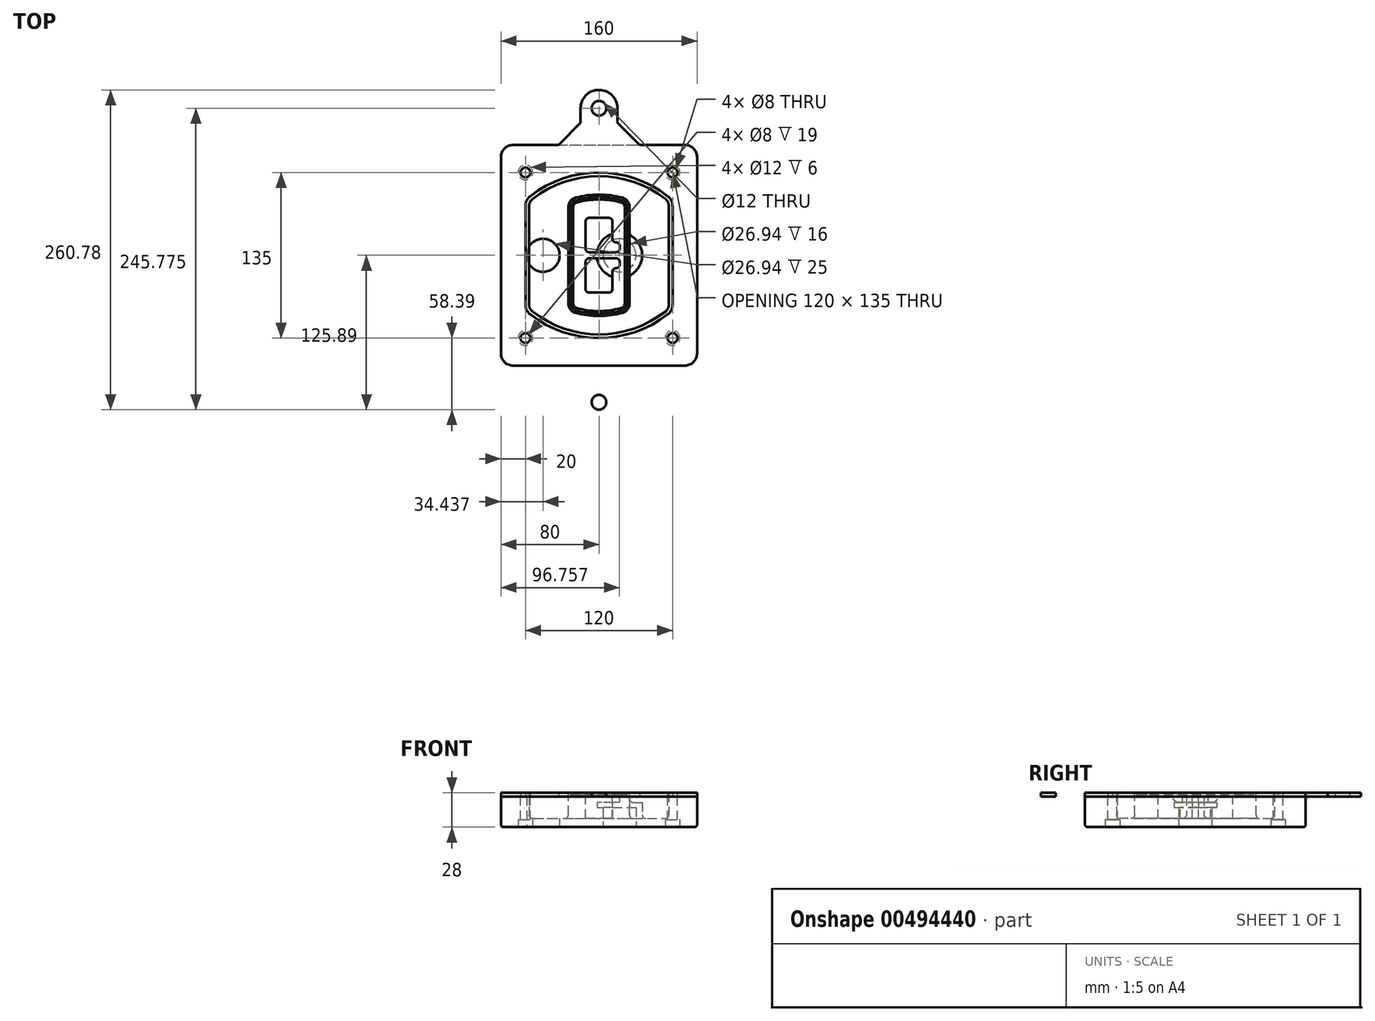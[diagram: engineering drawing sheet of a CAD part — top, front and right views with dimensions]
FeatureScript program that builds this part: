
annotation { "Feature Type Name" : "Feature", "Feature Type Description" : "" }
export const myFeature = defineFeature(function(context is Context, id is Id, definition is map)
    precondition{}
    {
        {
            var Q0;
            Q0=qCreatedBy(makeId("Top.planeOp"),FACE);
            var sketch = newSketch(context, id + "F0", { "sketchPlane" : qUnion([Q0])});
            skPoint(sketch, "E0.rect.middle", {"position": v(0, 0) * mm});
            skLineSegment(sketch, "E1.bottom", {"start": v(-70, -90) * mm, "end": v(70, -90) * mm});
            skLineSegment(sketch, "E1.top", {"start": v(-70, 90) * mm, "end": v(70, 90) * mm});
            skLineSegment(sketch, "E1.left", {"start": v(-80, -80) * mm, "end": v(-80, 80) * mm});
            skLineSegment(sketch, "E1.right", {"start": v(80, -80) * mm, "end": v(80, 80) * mm});
            skLineSegment(sketch, "E2", {"start": v(-80, 90) * mm, "end": v(80, -90) * mm, "construction": true});
            skLineSegment(sketch, "E3", {"start": v(80, 90) * mm, "end": v(-80, -90) * mm, "construction": true});
            skCircle(sketch, "E4", {"center": v(-60, 67.5) * mm, "radius": 4 * mm});
            skCircle(sketch, "E5", {"center": v(60, 67.5) * mm, "radius": 4 * mm});
            skCircle(sketch, "E6", {"center": v(60, -67.5) * mm, "radius": 4 * mm});
            skCircle(sketch, "E7", {"center": v(-60, -67.5) * mm, "radius": 4 * mm});
            skLineSegment(sketch, "E8", {"start": v(-60, 67.5) * mm, "end": v(60, 67.5) * mm, "construction": true});
            skLineSegment(sketch, "E9", {"start": v(60, 67.5) * mm, "end": v(60, -67.5) * mm, "construction": true});
            skLineSegment(sketch, "E10", {"start": v(60, -67.5) * mm, "end": v(-60, -67.5) * mm, "construction": true});
            skLineSegment(sketch, "E11", {"start": v(-60, -67.5) * mm, "end": v(-60, 67.5) * mm, "construction": true});
            skLineSegment(sketch, "E12", {"start": v(-60, 40.3) * mm, "end": v(-60, -40.3) * mm});
            skLineSegment(sketch, "E13", {"start": v(60, 40.3) * mm, "end": v(60, -40.3) * mm});
            skArc(sketch, "E14", {"start": v(56.15, 48.18) * mm, "mid": v(0, 67.5) * mm, "end": v(-56.15, 48.18) * mm});
            skArc(sketch, "E15", {"start": v(-56.15, -48.18) * mm, "mid": v(0, -67.5) * mm, "end": v(56.15, -48.18) * mm});
            skLineSegment(sketch, "E16", {"start": v(-60, 0) * mm, "end": v(60, 0) * mm, "construction": true});
            skPoint(sketch, "E17.visualSharp", {"position": v(-60, -45) * mm});
            skArc(sketch, "E17.filletArc", {"start": v(-60, -40.3) * mm, "mid": v(-58.99, -44.68) * mm, "end": v(-56.15, -48.18) * mm});
            skPoint(sketch, "E18.visualSharp", {"position": v(-60, 45) * mm});
            skArc(sketch, "E18.filletArc", {"start": v(-56.15, 48.18) * mm, "mid": v(-58.99, 44.68) * mm, "end": v(-60, 40.3) * mm});
            skPoint(sketch, "E19.visualSharp", {"position": v(60, 45) * mm});
            skArc(sketch, "E19.filletArc", {"start": v(60, 40.3) * mm, "mid": v(58.99, 44.68) * mm, "end": v(56.15, 48.18) * mm});
            skPoint(sketch, "E20.visualSharp", {"position": v(60, -45) * mm});
            skArc(sketch, "E20.filletArc", {"start": v(56.15, -48.18) * mm, "mid": v(58.99, -44.68) * mm, "end": v(60, -40.3) * mm});
            skPoint(sketch, "E21.visualSharp", {"position": v(-80, 90) * mm});
            skArc(sketch, "E21.filletArc", {"start": v(-70, 90) * mm, "mid": v(-77.07, 87.07) * mm, "end": v(-80, 80) * mm});
            skPoint(sketch, "E22.visualSharp", {"position": v(80, 90) * mm});
            skArc(sketch, "E22.filletArc", {"start": v(80, 80) * mm, "mid": v(77.07, 87.07) * mm, "end": v(70, 90) * mm});
            skPoint(sketch, "E23.visualSharp", {"position": v(80, -90) * mm});
            skArc(sketch, "E23.filletArc", {"start": v(70, -90) * mm, "mid": v(77.07, -87.07) * mm, "end": v(80, -80) * mm});
            skPoint(sketch, "E24.visualSharp", {"position": v(-80, -90) * mm});
            skArc(sketch, "E24.filletArc", {"start": v(-80, -80) * mm, "mid": v(-77.07, -87.07) * mm, "end": v(-70, -90) * mm});
            skArc(sketch, "E25.0", {"start": v(57, 40.3) * mm, "mid": v(56.3, 43.36) * mm, "end": v(54.3, 45.81) * mm});
            skLineSegment(sketch, "E25.1", {"start": v(57, 40.3) * mm, "end": v(57, -40.3) * mm});
            skArc(sketch, "E25.2", {"start": v(54.3, -45.81) * mm, "mid": v(56.3, -43.36) * mm, "end": v(57, -40.3) * mm});
            skArc(sketch, "E25.3", {"start": v(-54.3, -45.81) * mm, "mid": v(0, -64.5) * mm, "end": v(54.3, -45.81) * mm});
            skArc(sketch, "E25.4", {"start": v(-57, -40.3) * mm, "mid": v(-56.3, -43.36) * mm, "end": v(-54.3, -45.81) * mm});
            skArc(sketch, "E25.5", {"start": v(54.3, 45.81) * mm, "mid": v(0, 64.5) * mm, "end": v(-54.3, 45.81) * mm});
            skLineSegment(sketch, "E25.6", {"start": v(-57, 40.3) * mm, "end": v(-57, -40.3) * mm});
            skArc(sketch, "E25.7", {"start": v(-54.3, 45.81) * mm, "mid": v(-56.3, 43.36) * mm, "end": v(-57, 40.3) * mm});
            skArc(sketch, "E26.0", {"start": v(-58.62, 51.33) * mm, "mid": v(-62.58, 46.43) * mm, "end": v(-64, 40.3) * mm});
            skArc(sketch, "E26.1", {"start": v(58.62, 51.33) * mm, "mid": v(0, 71.5) * mm, "end": v(-58.62, 51.33) * mm});
            skArc(sketch, "E26.2", {"start": v(64, 40.3) * mm, "mid": v(62.58, 46.43) * mm, "end": v(58.62, 51.33) * mm});
            skLineSegment(sketch, "E26.3", {"start": v(64, 40.3) * mm, "end": v(64, -40.3) * mm});
            skArc(sketch, "E26.4", {"start": v(58.62, -51.33) * mm, "mid": v(62.58, -46.43) * mm, "end": v(64, -40.3) * mm});
            skLineSegment(sketch, "E26.5", {"start": v(-64, 40.3) * mm, "end": v(-64, -40.3) * mm});
            skArc(sketch, "E26.6", {"start": v(-58.62, -51.33) * mm, "mid": v(0, -71.5) * mm, "end": v(58.62, -51.33) * mm});
            skArc(sketch, "E26.7", {"start": v(-64, -40.3) * mm, "mid": v(-62.58, -46.43) * mm, "end": v(-58.62, -51.33) * mm});
            skSolve(sketch);
        }
        {
            var Q0;
            Q0=makeQuery(id+"F0.imprint","IMPRINT",FACE,{"disambiguationData":[TD([[makeQuery(id+"F0.imprint","IMPRINT",EDGE,{"derivedFrom":sQuery(id+"F0.wireOp",EDGE,"E1.bottom")}),1.0]])]});
            var Q1;
            Q1=makeQuery(id+"F0.imprint","IMPRINT",FACE,{"disambiguationData":[TD([[makeQuery(id+"F0.imprint","IMPRINT",EDGE,{"derivedFrom":sQuery(id+"F0.wireOp",EDGE,"E12")}),1.0]])]});
            var Q2;
            Q2=makeQuery(id+"F0.imprint","IMPRINT",FACE,{"disambiguationData":[TD([[makeQuery(id+"F0.imprint","IMPRINT",EDGE,{"derivedFrom":sQuery(id+"F0.wireOp",EDGE,"E25.0")}),1.0]])]});
            var Q3;
            Q3=makeQuery(id+"F0.imprint","IMPRINT",FACE,{"disambiguationData":[TD([[makeQuery(id+"F0.imprint","IMPRINT",EDGE,{"derivedFrom":sQuery(id+"F0.wireOp",EDGE,"E12")}),-1.0]])]});
            extrude(context, id + "F1", {"entities" : qUnion([Q0, Q1, Q2, Q3]), "oppositeDirection" : true, "depth" : 25 * mm});
        }
        {
            var Q0;
            Q0=makeQuery(id+"F0.imprint","IMPRINT",FACE,{"disambiguationData":[TD([[makeQuery(id+"F0.imprint","IMPRINT",EDGE,{"derivedFrom":sQuery(id+"F0.wireOp",EDGE,"E12")}),1.0]])]});
            extrude(context, id + "F2", {"entities" : qUnion([Q0]), "operationType" : NewBodyOperationType.ADD, "depth" : 3 * mm});
        }
        {
            var Q0;
            Q0=makeQuery(id+"F0.imprint","IMPRINT",FACE,{"disambiguationData":[TD([[makeQuery(id+"F0.imprint","IMPRINT",EDGE,{"derivedFrom":sQuery(id+"F0.wireOp",EDGE,"E25.0")}),1.0]])]});
            extrude(context, id + "F3", {"entities" : qUnion([Q0]), "operationType" : NewBodyOperationType.REMOVE, "oppositeDirection" : true, "depth" : 18 * mm});
        }
        {
            var Q0;
            Q0=makeQuery(id+"F2.opExtrude","CAP_FACE",FACE,{"disambiguationData":[OSD([sQuery(id+"F0.wireOp",EDGE,"E12"),sQuery(id+"F0.wireOp",EDGE,"E13"),sQuery(id+"F0.wireOp",EDGE,"E14"),sQuery(id+"F0.wireOp",EDGE,"E15"),sQuery(id+"F0.wireOp",EDGE,"E17.filletArc"),sQuery(id+"F0.wireOp",EDGE,"E18.filletArc"),sQuery(id+"F0.wireOp",EDGE,"E19.filletArc"),sQuery(id+"F0.wireOp",EDGE,"E20.filletArc"),sQuery(id+"F0.wireOp",EDGE,"E25.0"),sQuery(id+"F0.wireOp",EDGE,"E25.1"),sQuery(id+"F0.wireOp",EDGE,"E25.2"),sQuery(id+"F0.wireOp",EDGE,"E25.3"),sQuery(id+"F0.wireOp",EDGE,"E25.4"),sQuery(id+"F0.wireOp",EDGE,"E25.5"),sQuery(id+"F0.wireOp",EDGE,"E25.6"),sQuery(id+"F0.wireOp",EDGE,"E25.7")])],"isStart":false});
            var sketch = newSketch(context, id + "F4", { "sketchPlane" : qUnion([Q0])});
            skArc(sketch, "E27.0", {"start": v(-19.08, -46.97) * mm, "mid": v(0, -49.5) * mm, "end": v(19.08, -46.97) * mm});
            skArc(sketch, "E28.0", {"start": v(19.08, 46.97) * mm, "mid": v(0, 49.5) * mm, "end": v(-19.08, 46.97) * mm});
            skLineSegment(sketch, "E29", {"start": v(-25, 39.25) * mm, "end": v(-25, -39.25) * mm});
            skLineSegment(sketch, "E30", {"start": v(25, 39.25) * mm, "end": v(25, -39.25) * mm});
            skLineSegment(sketch, "E31", {"start": v(-25, 45.1) * mm, "end": v(25, 45.1) * mm, "construction": true});
            skLineSegment(sketch, "E32", {"start": v(-25, -45.1) * mm, "end": v(25, -45.1) * mm, "construction": true});
            skPoint(sketch, "E33.visualSharp", {"position": v(-25, 45.1) * mm});
            skArc(sketch, "E33.filletArc", {"start": v(-19.08, 46.97) * mm, "mid": v(-23.35, 44.11) * mm, "end": v(-25, 39.25) * mm});
            skPoint(sketch, "E34.visualSharp", {"position": v(25, 45.1) * mm});
            skArc(sketch, "E34.filletArc", {"start": v(25, 39.25) * mm, "mid": v(23.35, 44.11) * mm, "end": v(19.08, 46.97) * mm});
            skPoint(sketch, "E35.visualSharp", {"position": v(25, -45.1) * mm});
            skArc(sketch, "E35.filletArc", {"start": v(19.08, -46.97) * mm, "mid": v(23.35, -44.11) * mm, "end": v(25, -39.25) * mm});
            skPoint(sketch, "E36.visualSharp", {"position": v(-25, -45.1) * mm});
            skArc(sketch, "E36.filletArc", {"start": v(-25, -39.25) * mm, "mid": v(-23.35, -44.11) * mm, "end": v(-19.08, -46.97) * mm});
            skArc(sketch, "E37.0", {"start": v(54.3, 45.81) * mm, "mid": v(0, 64.5) * mm, "end": v(-54.3, 45.81) * mm});
            skArc(sketch, "E37.1", {"start": v(-54.3, 45.81) * mm, "mid": v(-56.3, 43.36) * mm, "end": v(-57, 40.3) * mm});
            skLineSegment(sketch, "E37.2", {"start": v(-57, 40.3) * mm, "end": v(-57, -40.3) * mm});
            skArc(sketch, "E37.3", {"start": v(-57, -40.3) * mm, "mid": v(-56.3, -43.36) * mm, "end": v(-54.3, -45.81) * mm});
            skArc(sketch, "E37.4", {"start": v(-54.3, -45.81) * mm, "mid": v(0, -64.5) * mm, "end": v(54.3, -45.81) * mm});
            skArc(sketch, "E37.5", {"start": v(54.3, -45.81) * mm, "mid": v(56.3, -43.36) * mm, "end": v(57, -40.3) * mm});
            skLineSegment(sketch, "E37.6", {"start": v(57, 40.3) * mm, "end": v(57, -40.3) * mm});
            skArc(sketch, "E37.7", {"start": v(57, 40.3) * mm, "mid": v(56.3, 43.36) * mm, "end": v(54.3, 45.81) * mm});
            skLineSegment(sketch, "E38.0", {"start": v(23, 39.25) * mm, "end": v(23, -39.25) * mm});
            skArc(sketch, "E38.1", {"start": v(18.56, -45.04) * mm, "mid": v(21.76, -42.9) * mm, "end": v(23, -39.25) * mm});
            skArc(sketch, "E38.2", {"start": v(-18.56, -45.04) * mm, "mid": v(0, -47.5) * mm, "end": v(18.56, -45.04) * mm});
            skArc(sketch, "E38.3", {"start": v(-23, -39.25) * mm, "mid": v(-21.76, -42.9) * mm, "end": v(-18.56, -45.04) * mm});
            skLineSegment(sketch, "E38.4", {"start": v(-23, 39.25) * mm, "end": v(-23, -39.25) * mm});
            skArc(sketch, "E38.5", {"start": v(23, 39.25) * mm, "mid": v(21.76, 42.9) * mm, "end": v(18.56, 45.04) * mm});
            skArc(sketch, "E38.6", {"start": v(-18.56, 45.04) * mm, "mid": v(-21.76, 42.9) * mm, "end": v(-23, 39.25) * mm});
            skArc(sketch, "E38.7", {"start": v(18.56, 45.04) * mm, "mid": v(0, 47.5) * mm, "end": v(-18.56, 45.04) * mm});
            skArc(sketch, "E39.0", {"start": v(21, 39.25) * mm, "mid": v(20.18, 41.68) * mm, "end": v(18.04, 43.1) * mm});
            skLineSegment(sketch, "E39.1", {"start": v(21, 39.25) * mm, "end": v(21, -39.25) * mm});
            skArc(sketch, "E39.2", {"start": v(18.04, -43.1) * mm, "mid": v(20.18, -41.68) * mm, "end": v(21, -39.25) * mm});
            skArc(sketch, "E39.3", {"start": v(-18.04, -43.1) * mm, "mid": v(0, -45.5) * mm, "end": v(18.04, -43.1) * mm});
            skArc(sketch, "E39.4", {"start": v(-21, -39.25) * mm, "mid": v(-20.18, -41.68) * mm, "end": v(-18.04, -43.1) * mm});
            skArc(sketch, "E39.5", {"start": v(18.04, 43.1) * mm, "mid": v(0, 45.5) * mm, "end": v(-18.04, 43.1) * mm});
            skLineSegment(sketch, "E39.6", {"start": v(-21, 39.25) * mm, "end": v(-21, -39.25) * mm});
            skArc(sketch, "E39.7", {"start": v(-18.04, 43.1) * mm, "mid": v(-20.18, 41.68) * mm, "end": v(-21, 39.25) * mm});
            skLineSegment(sketch, "E40", {"start": v(-25, 0) * mm, "end": v(25, 0) * mm, "construction": true});
            skLineSegment(sketch, "E41", {"start": v(-11, 5.5) * mm, "end": v(-11, 27.5) * mm});
            skLineSegment(sketch, "E42", {"start": v(-8, 30.5) * mm, "end": v(8, 30.5) * mm});
            skLineSegment(sketch, "E43", {"start": v(11, 27.5) * mm, "end": v(11, 13.5) * mm});
            skLineSegment(sketch, "E44", {"start": v(14, 10.5) * mm, "end": v(14, 10.5) * mm});
            skLineSegment(sketch, "E45", {"start": v(17, 7.5) * mm, "end": v(17, 5.5) * mm});
            skLineSegment(sketch, "E46", {"start": v(14, 2.5) * mm, "end": v(-8, 2.5) * mm});
            skPoint(sketch, "E47.visualSharp", {"position": v(-11, 30.5) * mm});
            skArc(sketch, "E47.filletArc", {"start": v(-8, 30.5) * mm, "mid": v(-10.12, 29.62) * mm, "end": v(-11, 27.5) * mm});
            skPoint(sketch, "E48.visualSharp", {"position": v(11, 30.5) * mm});
            skArc(sketch, "E48.filletArc", {"start": v(11, 27.5) * mm, "mid": v(10.12, 29.62) * mm, "end": v(8, 30.5) * mm});
            skPoint(sketch, "E49.visualSharp", {"position": v(11, 10.5) * mm});
            skArc(sketch, "E49.filletArc", {"start": v(11, 13.5) * mm, "mid": v(11.88, 11.38) * mm, "end": v(14, 10.5) * mm});
            skPoint(sketch, "E50.visualSharp", {"position": v(17, 10.5) * mm});
            skArc(sketch, "E50.filletArc", {"start": v(17, 7.5) * mm, "mid": v(16.12, 9.62) * mm, "end": v(14, 10.5) * mm});
            skPoint(sketch, "E51.visualSharp", {"position": v(17, 2.5) * mm});
            skArc(sketch, "E51.filletArc", {"start": v(14, 2.5) * mm, "mid": v(16.12, 3.38) * mm, "end": v(17, 5.5) * mm});
            skPoint(sketch, "E52.visualSharp", {"position": v(-11, 2.5) * mm});
            skArc(sketch, "E52.filletArc", {"start": v(-11, 5.5) * mm, "mid": v(-10.12, 3.38) * mm, "end": v(-8, 2.5) * mm});
            skLineSegment(sketch, "E53.0.MirrorCS", {"start": v(14, -2.5) * mm, "end": v(-8, -2.5) * mm});
            skArc(sketch, "E54.0.MirrorCS", {"start": v(-11, -5.5) * mm, "mid": v(-10.12, -3.38) * mm, "end": v(-8, -2.5) * mm});
            skLineSegment(sketch, "E55.0.MirrorCS", {"start": v(-11, -5.5) * mm, "end": v(-11, -27.5) * mm});
            skArc(sketch, "E56.0.MirrorCS", {"start": v(-8, -30.5) * mm, "mid": v(-10.12, -29.62) * mm, "end": v(-11, -27.5) * mm});
            skLineSegment(sketch, "E57.0.MirrorCS", {"start": v(-8, -30.5) * mm, "end": v(8, -30.5) * mm});
            skArc(sketch, "E58.0.MirrorCS", {"start": v(11, -27.5) * mm, "mid": v(10.12, -29.62) * mm, "end": v(8, -30.5) * mm});
            skLineSegment(sketch, "E59.0.MirrorCS", {"start": v(11, -27.5) * mm, "end": v(11, -13.5) * mm});
            skArc(sketch, "E60.0.MirrorCS", {"start": v(11, -13.5) * mm, "mid": v(11.88, -11.38) * mm, "end": v(14, -10.5) * mm});
            skArc(sketch, "E61.0.MirrorCS", {"start": v(17, -7.5) * mm, "mid": v(16.12, -9.62) * mm, "end": v(14, -10.5) * mm});
            skLineSegment(sketch, "E62.0.MirrorCS", {"start": v(17, -7.5) * mm, "end": v(17, -5.5) * mm});
            skArc(sketch, "E63.0.MirrorCS", {"start": v(14, -2.5) * mm, "mid": v(16.12, -3.38) * mm, "end": v(17, -5.5) * mm});
            skSolve(sketch);
        }
        {
            var Q0;
            Q0=makeQuery(id+"F4.imprint","IMPRINT",FACE,{"disambiguationData":[TD([[makeQuery(id+"F4.imprint","IMPRINT",EDGE,{"derivedFrom":sQuery(id+"F4.wireOp",EDGE,"E27.0")}),1.0]])]});
            var Q1;
            Q1=makeQuery(id+"F4.imprint","IMPRINT",FACE,{"disambiguationData":[TD([[makeQuery(id+"F4.imprint","IMPRINT",EDGE,{"derivedFrom":sQuery(id+"F4.wireOp",EDGE,"E38.0")}),-1.0]])]});
            var Q2;
            Q2=makeQuery(id+"F4.imprint","IMPRINT",FACE,{"disambiguationData":[TD([[makeQuery(id+"F4.imprint","IMPRINT",EDGE,{"derivedFrom":sQuery(id+"F4.wireOp",EDGE,"E39.0")}),1.0]])]});
            extrude(context, id + "F5", {"entities" : qUnion([Q0, Q1, Q2]), "operationType" : NewBodyOperationType.ADD, "endBound" : BoundingType.UP_TO_NEXT, "oppositeDirection" : true, "depth" : 25 * mm});
        }
        {
            var Q0;
            Q0=makeQuery(id+"F4.imprint","IMPRINT",FACE,{"disambiguationData":[TD([[makeQuery(id+"F4.imprint","IMPRINT",EDGE,{"derivedFrom":sQuery(id+"F4.wireOp",EDGE,"E38.0")}),-1.0]])]});
            extrude(context, id + "F6", {"entities" : qUnion([Q0]), "operationType" : NewBodyOperationType.REMOVE, "oppositeDirection" : true, "depth" : 2 * mm});
        }
        {
            var Q0;
            Q0=makeQuery(id+"F1.opExtrude","CAP_FACE",FACE,{"disambiguationData":[OSD([sQuery(id+"F0.wireOp",EDGE,"E1.bottom"),sQuery(id+"F0.wireOp",EDGE,"E1.top"),sQuery(id+"F0.wireOp",EDGE,"E1.left"),sQuery(id+"F0.wireOp",EDGE,"E1.right"),sQuery(id+"F0.wireOp",EDGE,"E4"),sQuery(id+"F0.wireOp",EDGE,"E5"),sQuery(id+"F0.wireOp",EDGE,"E6"),sQuery(id+"F0.wireOp",EDGE,"E7"),sQuery(id+"F0.wireOp",EDGE,"E21.filletArc"),sQuery(id+"F0.wireOp",EDGE,"E22.filletArc"),sQuery(id+"F0.wireOp",EDGE,"E23.filletArc"),sQuery(id+"F0.wireOp",EDGE,"E24.filletArc")])],"isStart":false});
            var sketch = newSketch(context, id + "F7", { "sketchPlane" : qUnion([Q0])});
            skCircle(sketch, "E64", {"center": v(16.76, 0) * mm, "radius": 13.47 * mm});
            skCircle(sketch, "E65", {"center": v(-45.56, 0) * mm, "radius": 13.47 * mm});
            skLineSegment(sketch, "E66", {"start": v(80, 0) * mm, "end": v(-80, 0) * mm});
            skCircle(sketch, "E67", {"center": v(16.76, 0) * mm, "radius": 18.47 * mm});
            skCircle(sketch, "E68", {"center": v(60, -67.5) * mm, "radius": 6 * mm});
            skCircle(sketch, "E69", {"center": v(-60, -67.5) * mm, "radius": 6 * mm});
            skCircle(sketch, "E70", {"center": v(-60, 67.5) * mm, "radius": 6 * mm});
            skCircle(sketch, "E71", {"center": v(60, 67.5) * mm, "radius": 6 * mm});
            skSolve(sketch);
        }
        {
            var Q0;
            {var subQ1=sQuery(id+"F7.wireOp",EDGE,"E66");var subQ4=sQuery(id+"F7.wireOp",EDGE,"E64");var subQ6=makeQuery(id+"F7.imprint","INTERSECT",VERTEX,{"disambiguationData":[OD(0.0)],"derivedFrom":[subQ4,subQ1]});Q0=makeQuery(id+"F7.imprint","IMPRINT",FACE,{"disambiguationData":[TD([[makeQuery(id+"F7.imprint","IMPRINT",EDGE,{"disambiguationData":[TD([[subQ6,-1.0]])],"derivedFrom":subQ4}),-1.0]])]});}
            var Q1;
            {var subQ0=sQuery(id+"F7.wireOp",EDGE,"E66");var subQ1=sQuery(id+"F7.wireOp",EDGE,"E64");var subQ3=makeQuery(id+"F7.imprint","INTERSECT",VERTEX,{"disambiguationData":[OD(0.0)],"derivedFrom":[subQ1,subQ0]});Q1=makeQuery(id+"F7.imprint","IMPRINT",FACE,{"disambiguationData":[TD([[makeQuery(id+"F7.imprint","IMPRINT",EDGE,{"disambiguationData":[TD([[subQ3,-1.0]])],"derivedFrom":subQ1}),1.0]])]});}
            var Q2;
            {var subQ0=sQuery(id+"F7.wireOp",EDGE,"E66");var subQ1=sQuery(id+"F7.wireOp",EDGE,"E64");var subQ3=makeQuery(id+"F7.imprint","INTERSECT",VERTEX,{"disambiguationData":[OD(0.0)],"derivedFrom":[subQ1,subQ0]});Q2=makeQuery(id+"F7.imprint","IMPRINT",FACE,{"disambiguationData":[TD([[makeQuery(id+"F7.imprint","IMPRINT",EDGE,{"disambiguationData":[TD([[subQ3,1.0]])],"derivedFrom":subQ1}),1.0]])]});}
            var Q3;
            {var subQ1=sQuery(id+"F7.wireOp",EDGE,"E66");var subQ4=sQuery(id+"F7.wireOp",EDGE,"E64");var subQ6=makeQuery(id+"F7.imprint","INTERSECT",VERTEX,{"disambiguationData":[OD(0.0)],"derivedFrom":[subQ4,subQ1]});Q3=makeQuery(id+"F7.imprint","IMPRINT",FACE,{"disambiguationData":[TD([[makeQuery(id+"F7.imprint","IMPRINT",EDGE,{"disambiguationData":[TD([[subQ6,1.0]])],"derivedFrom":subQ4}),-1.0]])]});}
            extrude(context, id + "F8", {"entities" : qUnion([Q0, Q1, Q2, Q3]), "operationType" : NewBodyOperationType.ADD, "oppositeDirection" : true, "depth" : 20 * mm});
        }
        {
            var Q0;
            {var subQ0=sQuery(id+"F7.wireOp",EDGE,"E66");var subQ1=sQuery(id+"F7.wireOp",EDGE,"E64");var subQ3=makeQuery(id+"F7.imprint","INTERSECT",VERTEX,{"disambiguationData":[OD(0.0)],"derivedFrom":[subQ1,subQ0]});Q0=makeQuery(id+"F7.imprint","IMPRINT",FACE,{"disambiguationData":[TD([[makeQuery(id+"F7.imprint","IMPRINT",EDGE,{"disambiguationData":[TD([[subQ3,-1.0]])],"derivedFrom":subQ1}),1.0]])]});}
            var Q1;
            {var subQ0=sQuery(id+"F7.wireOp",EDGE,"E66");var subQ1=sQuery(id+"F7.wireOp",EDGE,"E64");var subQ3=makeQuery(id+"F7.imprint","INTERSECT",VERTEX,{"disambiguationData":[OD(0.0)],"derivedFrom":[subQ1,subQ0]});Q1=makeQuery(id+"F7.imprint","IMPRINT",FACE,{"disambiguationData":[TD([[makeQuery(id+"F7.imprint","IMPRINT",EDGE,{"disambiguationData":[TD([[subQ3,1.0]])],"derivedFrom":subQ1}),1.0]])]});}
            extrude(context, id + "F9", {"entities" : qUnion([Q0, Q1]), "operationType" : NewBodyOperationType.REMOVE, "oppositeDirection" : true, "depth" : 16 * mm});
        }
        {
            var Q0;
            {var subQ0=sQuery(id+"F7.wireOp",EDGE,"E66");var subQ1=sQuery(id+"F7.wireOp",EDGE,"E65");var subQ3=makeQuery(id+"F7.imprint","INTERSECT",VERTEX,{"disambiguationData":[OD(0.0)],"derivedFrom":[subQ1,subQ0]});Q0=makeQuery(id+"F7.imprint","IMPRINT",FACE,{"disambiguationData":[TD([[makeQuery(id+"F7.imprint","IMPRINT",EDGE,{"disambiguationData":[TD([[subQ3,-1.0]])],"derivedFrom":subQ1}),1.0]])]});}
            var Q1;
            {var subQ0=sQuery(id+"F7.wireOp",EDGE,"E66");var subQ1=sQuery(id+"F7.wireOp",EDGE,"E65");var subQ3=makeQuery(id+"F7.imprint","INTERSECT",VERTEX,{"disambiguationData":[OD(0.0)],"derivedFrom":[subQ1,subQ0]});Q1=makeQuery(id+"F7.imprint","IMPRINT",FACE,{"disambiguationData":[TD([[makeQuery(id+"F7.imprint","IMPRINT",EDGE,{"disambiguationData":[TD([[subQ3,1.0]])],"derivedFrom":subQ1}),1.0]])]});}
            extrude(context, id + "F10", {"entities" : qUnion([Q0, Q1]), "operationType" : NewBodyOperationType.REMOVE, "oppositeDirection" : true, "depth" : 25 * mm});
        }
        {
            var Q0;
            Q0=makeQuery(id+"F7.imprint","IMPRINT",FACE,{"disambiguationData":[TD([[makeQuery(id+"F7.imprint","IMPRINT",EDGE,{"derivedFrom":sQuery(id+"F7.wireOp",EDGE,"E68")}),1.0]])]});
            var Q1;
            Q1=makeQuery(id+"F7.imprint","IMPRINT",FACE,{"disambiguationData":[TD([[makeQuery(id+"F7.imprint","IMPRINT",EDGE,{"derivedFrom":makeQuery(id+"F1.opExtrude","CAP_EDGE",EDGE,{"disambiguationData":[OSD([sQuery(id+"F0.wireOp",EDGE,"E5")])],"isStart":false})}),-1.0]])]});
            var Q2;
            Q2=makeQuery(id+"F7.imprint","IMPRINT",FACE,{"disambiguationData":[TD([[makeQuery(id+"F7.imprint","IMPRINT",EDGE,{"derivedFrom":sQuery(id+"F7.wireOp",EDGE,"E69")}),1.0]])]});
            var Q3;
            Q3=makeQuery(id+"F7.imprint","IMPRINT",FACE,{"disambiguationData":[TD([[makeQuery(id+"F7.imprint","IMPRINT",EDGE,{"derivedFrom":makeQuery(id+"F1.opExtrude","CAP_EDGE",EDGE,{"disambiguationData":[OSD([sQuery(id+"F0.wireOp",EDGE,"E4")])],"isStart":false})}),-1.0]])]});
            var Q4;
            Q4=makeQuery(id+"F7.imprint","IMPRINT",FACE,{"disambiguationData":[TD([[makeQuery(id+"F7.imprint","IMPRINT",EDGE,{"derivedFrom":sQuery(id+"F7.wireOp",EDGE,"E70")}),1.0]])]});
            var Q5;
            Q5=makeQuery(id+"F7.imprint","IMPRINT",FACE,{"disambiguationData":[TD([[makeQuery(id+"F7.imprint","IMPRINT",EDGE,{"derivedFrom":makeQuery(id+"F1.opExtrude","CAP_EDGE",EDGE,{"disambiguationData":[OSD([sQuery(id+"F0.wireOp",EDGE,"E7")])],"isStart":false})}),-1.0]])]});
            var Q6;
            Q6=makeQuery(id+"F7.imprint","IMPRINT",FACE,{"disambiguationData":[TD([[makeQuery(id+"F7.imprint","IMPRINT",EDGE,{"derivedFrom":sQuery(id+"F7.wireOp",EDGE,"E71")}),1.0]])]});
            var Q7;
            Q7=makeQuery(id+"F7.imprint","IMPRINT",FACE,{"disambiguationData":[TD([[makeQuery(id+"F7.imprint","IMPRINT",EDGE,{"derivedFrom":makeQuery(id+"F1.opExtrude","CAP_EDGE",EDGE,{"disambiguationData":[OSD([sQuery(id+"F0.wireOp",EDGE,"E6")])],"isStart":false})}),-1.0]])]});
            extrude(context, id + "F11", {"entities" : qUnion([Q0, Q1, Q2, Q3, Q4, Q5, Q6, Q7]), "operationType" : NewBodyOperationType.REMOVE, "oppositeDirection" : true, "depth" : 6 * mm});
        }
        {
            var Q0;
            Q0=makeQuery(id+"F9.boolean.opBoolean","COPY",FACE,{"derivedFrom":makeQuery(id+"F9.opExtrude","CAP_FACE",FACE,{"disambiguationData":[OSD([sQuery(id+"F7.wireOp",EDGE,"E64")])],"isStart":false})});
            var sketch = newSketch(context, id + "F12", { "sketchPlane" : qUnion([Q0])});
            skArc(sketch, "E72.0", {"start": v(11, 17.55) * mm, "mid": v(2.57, 11.82) * mm, "end": v(-1.54, 2.5) * mm});
            skArc(sketch, "E72.1", {"start": v(-1.54, -2.5) * mm, "mid": v(2.57, -11.82) * mm, "end": v(11, -17.55) * mm});
            skLineSegment(sketch, "E73", {"start": v(-1.54, -2.5) * mm, "end": v(14, -2.5) * mm});
            skLineSegment(sketch, "E74.0", {"start": v(14, 2.5) * mm, "end": v(-1.54, 2.5) * mm});
            skArc(sketch, "E74.1", {"start": v(14, 2.5) * mm, "mid": v(16.12, 3.38) * mm, "end": v(17, 5.5) * mm});
            skLineSegment(sketch, "E74.2", {"start": v(17, 7.5) * mm, "end": v(17, 5.5) * mm});
            skArc(sketch, "E74.3", {"start": v(17, 7.5) * mm, "mid": v(16.12, 9.62) * mm, "end": v(14, 10.5) * mm});
            skArc(sketch, "E74.4", {"start": v(11, 13.5) * mm, "mid": v(11.88, 11.38) * mm, "end": v(14, 10.5) * mm});
            skLineSegment(sketch, "E74.5", {"start": v(11, 17.55) * mm, "end": v(11, 13.5) * mm});
            skLineSegment(sketch, "E74.7", {"start": v(14, -2.5) * mm, "end": v(-1.54, -2.5) * mm});
            skArc(sketch, "E74.8", {"start": v(14, -2.5) * mm, "mid": v(16.12, -3.38) * mm, "end": v(17, -5.5) * mm});
            skLineSegment(sketch, "E74.9", {"start": v(17, -7.5) * mm, "end": v(17, -5.5) * mm});
            skArc(sketch, "E74.10", {"start": v(17, -7.5) * mm, "mid": v(16.12, -9.62) * mm, "end": v(14, -10.5) * mm});
            skArc(sketch, "E74.11", {"start": v(11, -13.5) * mm, "mid": v(11.88, -11.38) * mm, "end": v(14, -10.5) * mm});
            skLineSegment(sketch, "E74.12", {"start": v(11, -17.55) * mm, "end": v(11, -13.5) * mm});
            skPoint(sketch, "E75.orphan", {"position": v(11, -27.5) * mm});
            skPoint(sketch, "E76.orphan", {"position": v(-8, -2.5) * mm});
            skPoint(sketch, "E77.orphan", {"position": v(-8, 2.5) * mm});
            skPoint(sketch, "E78.orphan", {"position": v(11, 27.5) * mm});
            skSolve(sketch);
        }
        {
            var Q0;
            {var subQ7=sQuery(id+"F12.wireOp",EDGE,"E72.0");var subQ14=sQuery(id+"F12.wireOp",EDGE,"E72.1");var subQ16=sQuery(id+"F12.wireOp",EDGE,"E74.1");var subQ18=sQuery(id+"F12.wireOp",EDGE,"E74.8");Q0=qUnion([makeQuery(id+"F12.imprint","IMPRINT",FACE,{"disambiguationData":[TD([[makeQuery(id+"F12.imprint","IMPRINT",EDGE,{"derivedFrom":subQ7}),1.0]])]}),makeQuery(id+"F12.imprint","IMPRINT",FACE,{"disambiguationData":[TD([[makeQuery(id+"F12.imprint","IMPRINT",EDGE,{"derivedFrom":subQ14}),1.0]])]}),makeQuery(id+"F12.imprint","IMPRINT",FACE,{"disambiguationData":[TD([[makeQuery(id+"F12.imprint","IMPRINT",EDGE,{"derivedFrom":subQ16}),1.0]])]}),makeQuery(id+"F12.imprint","IMPRINT",FACE,{"disambiguationData":[TD([[makeQuery(id+"F12.imprint","IMPRINT",EDGE,{"derivedFrom":subQ18}),-1.0]])]})]);}
            var Q1;
            Q1=makeQuery(id+"F5.boolean.opBoolean","SPLIT",FACE,{"disambiguationData":[TD([makeQuery(id+"F5.opExtrude","SWEPT_FACE",FACE,{"disambiguationData":[OSD([sQuery(id+"F4.wireOp",EDGE,"E41")])]})])],"derivedFrom":makeQuery(id+"F3.boolean.opBoolean","COPY",FACE,{"derivedFrom":makeQuery(id+"F3.opExtrude","CAP_FACE",FACE,{"disambiguationData":[OSD([sQuery(id+"F0.wireOp",EDGE,"E25.0"),sQuery(id+"F0.wireOp",EDGE,"E25.1"),sQuery(id+"F0.wireOp",EDGE,"E25.2"),sQuery(id+"F0.wireOp",EDGE,"E25.3"),sQuery(id+"F0.wireOp",EDGE,"E25.4"),sQuery(id+"F0.wireOp",EDGE,"E25.5"),sQuery(id+"F0.wireOp",EDGE,"E25.6"),sQuery(id+"F0.wireOp",EDGE,"E25.7")])],"isStart":false})})});
            extrude(context, id + "F13", {"entities" : qUnion([Q0]), "operationType" : NewBodyOperationType.REMOVE, "endBound" : BoundingType.UP_TO_SURFACE, "endBoundEntityFace" : qUnion([Q1]), "depth" : 25 * mm});
        }
        {
            var Q0;
            Q0=makeQuery(id+"F3.boolean.opBoolean","COPY",EDGE,{"derivedFrom":makeQuery(id+"F3.opExtrude","CAP_EDGE",EDGE,{"disambiguationData":[OSD([sQuery(id+"F0.wireOp",EDGE,"E25.6")])],"isStart":false})});
            var Q1;
            Q1=makeQuery(id+"F8.boolean.opBoolean","INTERSECT",EDGE,{"derivedFrom":[makeQuery(id+"F5.opExtrude","SWEPT_FACE",FACE,{"disambiguationData":[OSD([sQuery(id+"F4.wireOp",EDGE,"E30")])]}),makeQuery(id+"F8.opExtrude","CAP_FACE",FACE,{"disambiguationData":[OSD([sQuery(id+"F7.wireOp",EDGE,"E67")])],"isStart":false})]});
            var Q2;
            Q2=makeQuery(id+"F8.boolean.opBoolean","INTERSECT",EDGE,{"disambiguationData":[OD(1.0)],"derivedFrom":[makeQuery(id+"F5.opExtrude","SWEPT_FACE",FACE,{"disambiguationData":[OSD([sQuery(id+"F4.wireOp",EDGE,"E30")])]}),makeQuery(id+"F8.opExtrude","SWEPT_FACE",FACE,{"disambiguationData":[OSD([sQuery(id+"F7.wireOp",EDGE,"E67")])]})]});
            var Q3;
            {var subQ0=sQuery(id+"F4.wireOp",EDGE,"E30");Q3=makeQuery(id+"F8.boolean.opBoolean","SPLIT",EDGE,{"disambiguationData":[TD([makeQuery(id+"F5.opExtrude","SWEPT_FACE",FACE,{"disambiguationData":[OSD([sQuery(id+"F4.wireOp",EDGE,"E35.filletArc")])]})])],"derivedFrom":makeQuery(id+"F5.opExtrude","CAP_EDGE",EDGE,{"disambiguationData":[OSD([subQ0])],"isStart":false})});}
            var Q4;
            {var subQ0=sQuery(id+"F0.wireOp",EDGE,"E25.7");var subQ1=sQuery(id+"F0.wireOp",EDGE,"E25.1");var subQ2=sQuery(id+"F0.wireOp",EDGE,"E25.6");var subQ3=sQuery(id+"F0.wireOp",EDGE,"E25.5");var subQ4=sQuery(id+"F0.wireOp",EDGE,"E25.4");var subQ5=sQuery(id+"F0.wireOp",EDGE,"E25.0");var subQ6=sQuery(id+"F0.wireOp",EDGE,"E25.2");var subQ7=sQuery(id+"F0.wireOp",EDGE,"E25.3");Q4=makeQuery(id+"F8.boolean.opBoolean","INTERSECT",EDGE,{"derivedFrom":[makeQuery(id+"F5.boolean.opBoolean","SPLIT",FACE,{"disambiguationData":[TD([makeQuery(id+"F2.opExtrude","SWEPT_FACE",FACE,{"disambiguationData":[OSD([subQ5])]})])],"derivedFrom":makeQuery(id+"F3.boolean.opBoolean","COPY",FACE,{"derivedFrom":makeQuery(id+"F3.opExtrude","CAP_FACE",FACE,{"disambiguationData":[OSD([subQ5,subQ1,subQ6,subQ7,subQ4,subQ3,subQ2,subQ0])],"isStart":false})})}),makeQuery(id+"F8.opExtrude","SWEPT_FACE",FACE,{"disambiguationData":[OSD([sQuery(id+"F7.wireOp",EDGE,"E67")])]})]});}
            var Q5;
            Q5=makeQuery(id+"F8.boolean.opBoolean","INTERSECT",EDGE,{"disambiguationData":[OD(0.0)],"derivedFrom":[makeQuery(id+"F5.opExtrude","SWEPT_FACE",FACE,{"disambiguationData":[OSD([sQuery(id+"F4.wireOp",EDGE,"E30")])]}),makeQuery(id+"F8.opExtrude","SWEPT_FACE",FACE,{"disambiguationData":[OSD([sQuery(id+"F7.wireOp",EDGE,"E67")])]})]});
            fillet(context, id + "F14", {"entities" : qUnion([Q0, Q1, Q2, Q3, Q4, Q5]), "radius" : 3 * mm, "tangentPropagation" : true, "allowEdgeOverflow" : false});
        }
        {
            var Q0;
            Q0=makeQuery(id+"F1.opExtrude","CAP_EDGE",EDGE,{"disambiguationData":[OSD([sQuery(id+"F0.wireOp",EDGE,"E1.bottom")])],"isStart":false});
            fillet(context, id + "F15", {"entities" : qUnion([Q0]), "radius" : 2 * mm, "tangentPropagation" : true, "allowEdgeOverflow" : false});
        }
        {
            var Q0;
            {var subQ0=sQuery(id+"F0.wireOp",EDGE,"E21.filletArc");var subQ1=sQuery(id+"F0.wireOp",EDGE,"E7");var subQ2=sQuery(id+"F0.wireOp",EDGE,"E6");var subQ3=sQuery(id+"F0.wireOp",EDGE,"E5");var subQ4=sQuery(id+"F0.wireOp",EDGE,"E4");var subQ5=sQuery(id+"F0.wireOp",EDGE,"E22.filletArc");var subQ6=sQuery(id+"F0.wireOp",EDGE,"E1.bottom");var subQ7=sQuery(id+"F0.wireOp",EDGE,"E1.right");var subQ8=sQuery(id+"F0.wireOp",EDGE,"E1.top");var subQ9=sQuery(id+"F0.wireOp",EDGE,"E1.left");var subQ10=sQuery(id+"F0.wireOp",EDGE,"E23.filletArc");var subQ11=sQuery(id+"F0.wireOp",EDGE,"E24.filletArc");Q0=makeQuery(id+"F2.boolean.opBoolean","SPLIT",FACE,{"disambiguationData":[TD([makeQuery(id+"F1.opExtrude","SWEPT_FACE",FACE,{"disambiguationData":[OSD([subQ6])]})])],"derivedFrom":makeQuery(id+"F1.opExtrude","CAP_FACE",FACE,{"disambiguationData":[OSD([subQ6,subQ8,subQ9,subQ7,subQ4,subQ3,subQ2,subQ1,subQ0,subQ5,subQ10,subQ11])],"isStart":true})});}
            var sketch = newSketch(context, id + "F16", { "sketchPlane" : qUnion([Q0])});
            skLineSegment(sketch, "E79", {"start": v(0, 90) * mm, "end": v(0, 119.89) * mm, "construction": true});
            skLineSegment(sketch, "E80", {"start": v(0, 90) * mm, "end": v(-33, 90) * mm});
            skLineSegment(sketch, "E81", {"start": v(0, 90) * mm, "end": v(33, 90) * mm});
            skLineSegment(sketch, "E82", {"start": v(33, 90) * mm, "end": v(15, 108) * mm});
            skLineSegment(sketch, "E83", {"start": v(-33, 90) * mm, "end": v(-15, 108) * mm});
            skLineSegment(sketch, "E84", {"start": v(-15, 120) * mm, "end": v(-15, 108) * mm});
            skLineSegment(sketch, "E85", {"start": v(15, 108) * mm, "end": v(15, 119.89) * mm});
            skArc(sketch, "E86", {"start": v(15, 119.89) * mm, "mid": v(0.06, 134.89) * mm, "end": v(-15, 120) * mm});
            skCircle(sketch, "E87", {"center": v(0, 119.89) * mm, "radius": 6 * mm});
            skLineSegment(sketch, "E88", {"start": v(-80, 0) * mm, "end": v(80, 0) * mm, "construction": true});
            skCircle(sketch, "E89.MirrorC", {"center": v(0, -119.89) * mm, "radius": 6 * mm});
            skLineSegment(sketch, "E90.MirrorCS", {"start": v(0, -90) * mm, "end": v(0, -119.89) * mm, "construction": true});
            skLineSegment(sketch, "E91.MirrorCS", {"start": v(0, -90) * mm, "end": v(-33, -90) * mm});
            skLineSegment(sketch, "E92.MirrorCS", {"start": v(-15, -120) * mm, "end": v(-15, -108) * mm});
            skLineSegment(sketch, "E93.MirrorCS", {"start": v(0, -90) * mm, "end": v(33, -90) * mm});
            skLineSegment(sketch, "E94.MirrorCS", {"start": v(33, -90) * mm, "end": v(15, -108) * mm});
            skLineSegment(sketch, "E95.MirrorCS", {"start": v(-33, -90) * mm, "end": v(-15, -108) * mm});
            skLineSegment(sketch, "E96.MirrorCS", {"start": v(15, -108) * mm, "end": v(15, -119.89) * mm});
            skArc(sketch, "E97.MirrorCS", {"start": v(15, -119.89) * mm, "mid": v(0.06, -134.89) * mm, "end": v(-15, -120) * mm});
            skSolve(sketch);
        }
        {
            var Q0;
            Q0=makeQuery(id+"F16.imprint","IMPRINT",FACE,{"disambiguationData":[TD([[makeQuery(id+"F16.imprint","IMPRINT",EDGE,{"derivedFrom":sQuery(id+"F16.wireOp",EDGE,"E89.MirrorC")}),1.0]])]});
            var Q1;
            {var subQ5=sQuery(id+"F16.wireOp",EDGE,"E80");Q1=makeQuery(id+"F16.imprint","IMPRINT",FACE,{"disambiguationData":[TD([[makeQuery(id+"F16.imprint","IMPRINT",EDGE,{"derivedFrom":subQ5}),-1.0]])]});}
            var Q2;
            Q2=makeQuery(id+"F16.imprint","IMPRINT",FACE,{"disambiguationData":[TD([[makeQuery(id+"F16.imprint","IMPRINT",EDGE,{"derivedFrom":sQuery(id+"F16.wireOp",EDGE,"E80")}),1.0]])]});
            var Q3;
            Q3=makeQuery(id+"F2.opExtrude","CAP_FACE",FACE,{"disambiguationData":[OSD([sQuery(id+"F0.wireOp",EDGE,"E12"),sQuery(id+"F0.wireOp",EDGE,"E13"),sQuery(id+"F0.wireOp",EDGE,"E14"),sQuery(id+"F0.wireOp",EDGE,"E15"),sQuery(id+"F0.wireOp",EDGE,"E17.filletArc"),sQuery(id+"F0.wireOp",EDGE,"E18.filletArc"),sQuery(id+"F0.wireOp",EDGE,"E19.filletArc"),sQuery(id+"F0.wireOp",EDGE,"E20.filletArc"),sQuery(id+"F0.wireOp",EDGE,"E25.0"),sQuery(id+"F0.wireOp",EDGE,"E25.1"),sQuery(id+"F0.wireOp",EDGE,"E25.2"),sQuery(id+"F0.wireOp",EDGE,"E25.3"),sQuery(id+"F0.wireOp",EDGE,"E25.4"),sQuery(id+"F0.wireOp",EDGE,"E25.5"),sQuery(id+"F0.wireOp",EDGE,"E25.6"),sQuery(id+"F0.wireOp",EDGE,"E25.7")])],"isStart":false});
            extrude(context, id + "F17", {"entities" : qUnion([Q0, Q1, Q2]), "endBound" : BoundingType.UP_TO_SURFACE, "endBoundEntityFace" : qUnion([Q3]), "depth" : 5 * mm});
        }
    });
